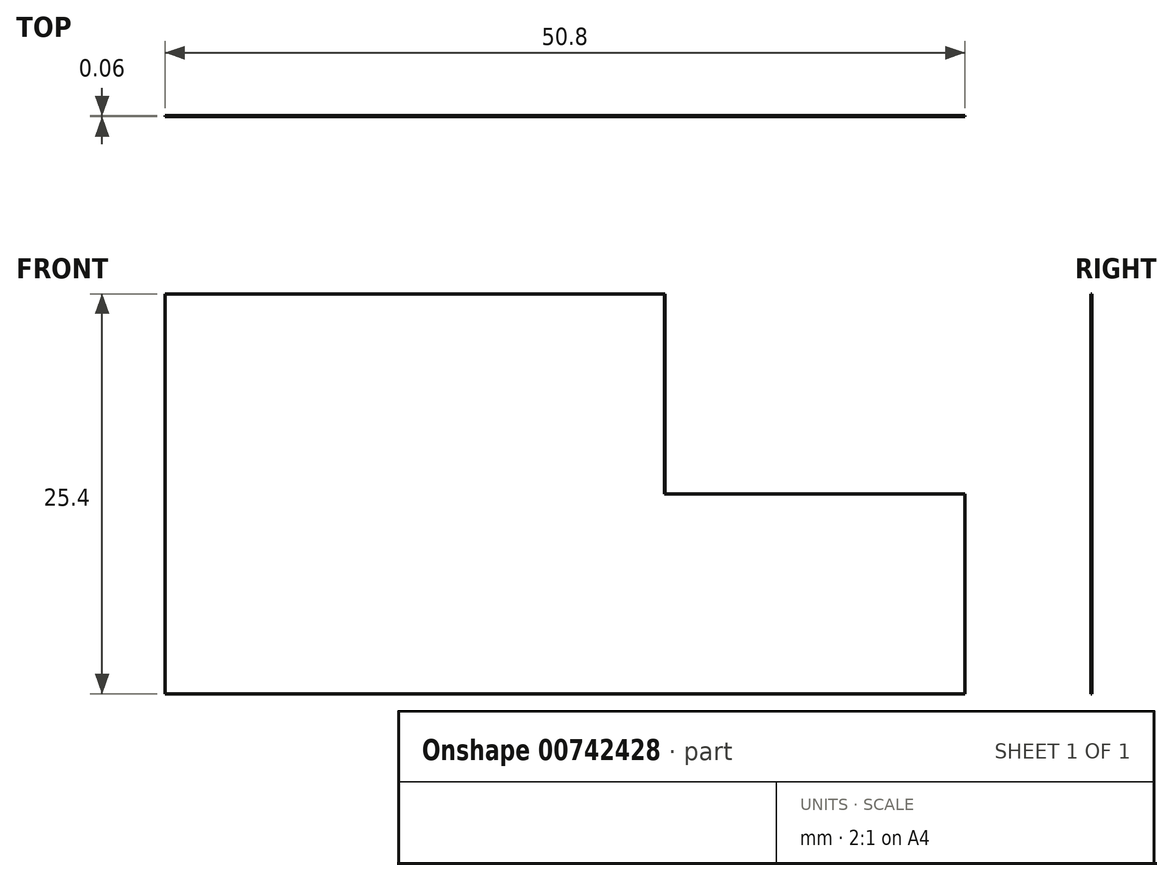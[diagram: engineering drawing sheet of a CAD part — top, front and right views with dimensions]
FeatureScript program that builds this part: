
annotation { "Feature Type Name" : "Feature", "Feature Type Description" : "" }
export const myFeature = defineFeature(function(context is Context, id is Id, definition is map)
    precondition{}
    {
        {
            var Q0;
            Q0=qCreatedBy(makeId("Front.planeOp"),FACE);
            var sketch = newSketch(context, id + "F0", { "sketchPlane" : qUnion([Q0])});
            skLineSegment(sketch, "E0", {"start": v(0, 0) * mm, "end": v(0, 25.4) * mm});
            skLineSegment(sketch, "E1", {"start": v(0, 25.4) * mm, "end": v(50.8, 25.4) * mm});
            skLineSegment(sketch, "E2", {"start": v(50.8, 25.4) * mm, "end": v(50.8, 0) * mm});
            skLineSegment(sketch, "E3", {"start": v(50.8, 0) * mm, "end": v(0, 0) * mm});
            skSolve(sketch);
        }
        {
            var Q0;
            Q0 = qSketchRegion(id + "F0", true);
            extrude(context, id + "F1", {"entities" : qUnion([Q0]), "depth" : 6 / 101.6 * mm, "offsetDistance" : 25.4 * mm});
        }
        {
            var Q0;
            Q0=makeQuery(id+"F1.opExtrude","SWEPT_FACE",FACE,{"disambiguationData":[OSD([sQuery(id+"F0.wireOp",EDGE,"E1")])]});
            var sketch = newSketch(context, id + "F2", { "sketchPlane" : qUnion([Q0])});
            skLineSegment(sketch, "E4", {"start": v(6.35, -38.1) * mm, "end": v(31.75, 0) * mm});
            skLineSegment(sketch, "E5", {"start": v(6.35, -38.1) * mm, "end": v(38.1, -38.1) * mm});
            skLineSegment(sketch, "E6", {"start": v(38.1, -38.1) * mm, "end": v(50.8, -19.05) * mm});
            skLineSegment(sketch, "E7", {"start": v(50.8, -19.05) * mm, "end": v(50.8, 0) * mm});
            skLineSegment(sketch, "E8", {"start": v(50.8, 0) * mm, "end": v(31.75, 0) * mm});
            skSolve(sketch);
        }
        {
            var Q0;
            Q0=makeQuery(id+"F2.imprint","IMPRINT",FACE,{"disambiguationData":[TD([[makeQuery(id+"F2.imprint","IMPRINT",EDGE,{"derivedFrom":sQuery(id+"F2.wireOp",EDGE,"E4")}),-1.0]])]});
            extrude(context, id + "F3", {"entities" : qUnion([Q0]), "operationType" : NewBodyOperationType.REMOVE, "oppositeDirection" : true, "depth" : 12.7 * mm, "offsetDistance" : 25.4 * mm});
        }
    });
